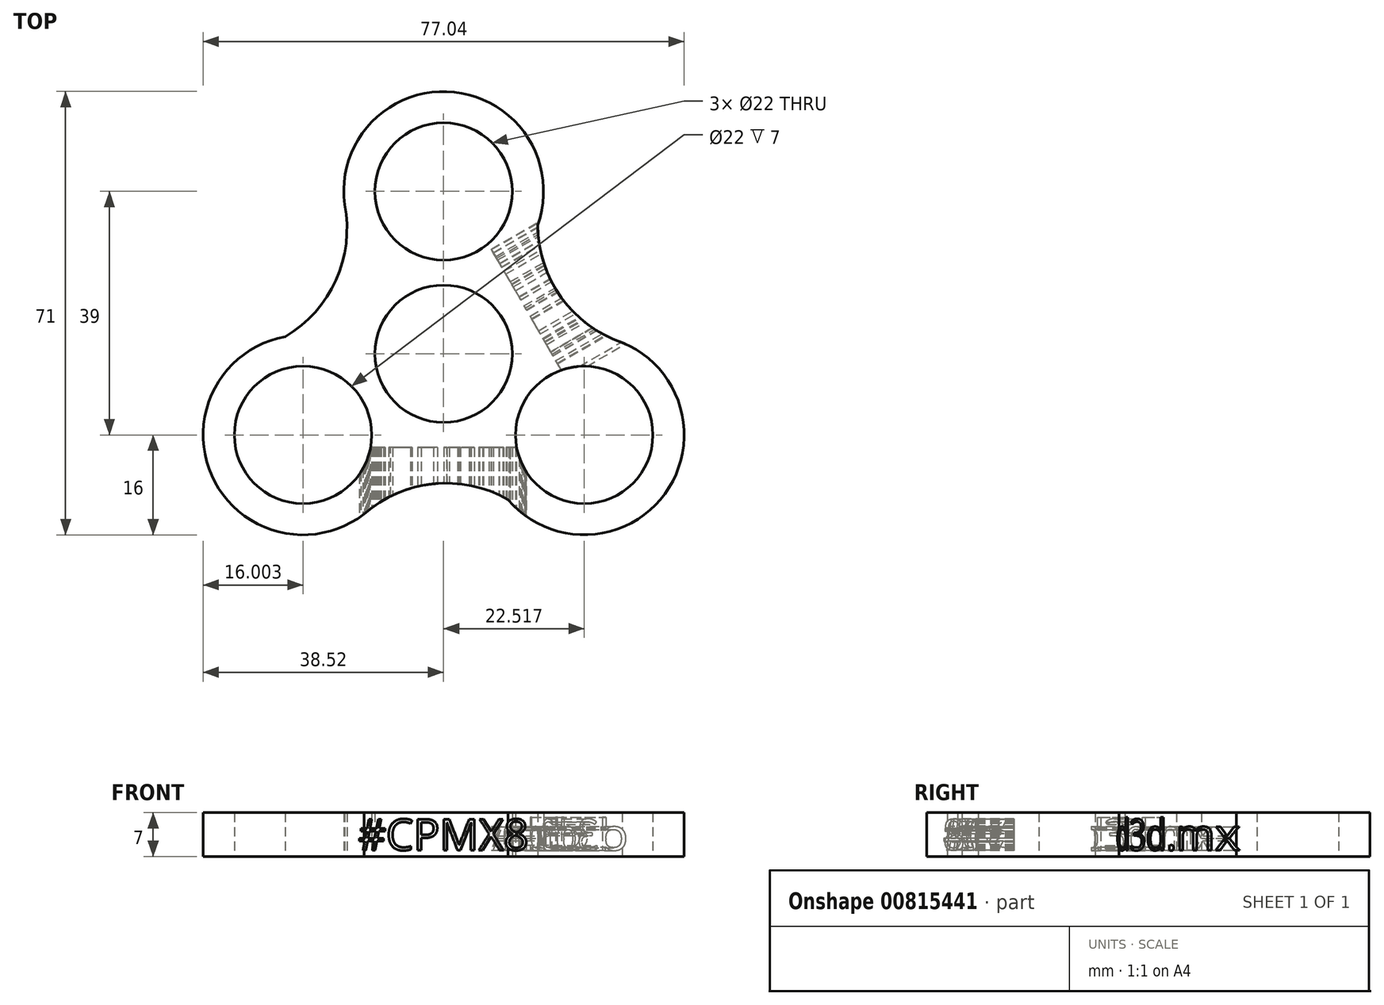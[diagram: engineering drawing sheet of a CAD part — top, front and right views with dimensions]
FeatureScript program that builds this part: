
annotation { "Feature Type Name" : "Feature", "Feature Type Description" : "" }
export const myFeature = defineFeature(function(context is Context, id is Id, definition is map)
    precondition{}
    {
        {
            var Q0;
            Q0=qCreatedBy(makeId("Top.planeOp"),FACE);
            var sketch = newSketch(context, id + "F0", { "sketchPlane" : qUnion([Q0])});
            skCircle(sketch, "E0", {"center": v(0, 0) * mm, "radius": 11 * mm});
            skCircle(sketch, "E1", {"center": v(0, 26) * mm, "radius": 11 * mm});
            skCircle(sketch, "E2.1.0", {"center": v(-22.52, -13) * mm, "radius": 11 * mm});
            skCircle(sketch, "E2.2.0", {"center": v(22.52, -13) * mm, "radius": 11 * mm});
            skArc(sketch, "E3", {"start": v(15.07, 20.61) * mm, "mid": v(1.13, 41.96) * mm, "end": v(-15.67, 22.78) * mm});
            skArc(sketch, "E4.1.0", {"start": v(-25.38, 2.74) * mm, "mid": v(-36.9, -20) * mm, "end": v(-11.9, -24.96) * mm});
            skArc(sketch, "E4.2.0", {"start": v(10.32, -23.35) * mm, "mid": v(35.77, -21.96) * mm, "end": v(27.57, 2.18) * mm});
            skArc(sketch, "E5", {"start": v(-25.38, 2.74) * mm, "mid": v(-17.24, 11.8) * mm, "end": v(-15.86, 23.89) * mm});
            skPoint(sketch, "E5.first.point", {"position": v(-25.38, 2.74) * mm});
            skPoint(sketch, "E5.second.point", {"position": v(-15.67, 22.78) * mm});
            skPoint(sketch, "E5.third.point", {"position": v(-55.07, 24.02) * mm});
            skArc(sketch, "E6.1.0", {"start": v(10.32, -23.35) * mm, "mid": v(-1.6, -20.83) * mm, "end": v(-12.76, -25.68) * mm});
            skArc(sketch, "E6.2.0", {"start": v(15.07, 20.61) * mm, "mid": v(18.84, 9.04) * mm, "end": v(28.62, 1.8) * mm});
            skSolve(sketch);
        }
        {
            var Q0;
            Q0=makeQuery(id+"F0.imprint","IMPRINT",FACE,{"disambiguationData":[TD([[makeQuery(id+"F0.imprint","IMPRINT",EDGE,{"derivedFrom":sQuery(id+"F0.wireOp",EDGE,"E0")}),-1.0]])]});
            extrude(context, id + "F1", {"entities" : qUnion([Q0]), "depth" : 7 * mm, "offsetDistance" : 25 * mm});
        }
        {
            var Q0;
            Q0=qCreatedBy(makeId("Front.planeOp"),FACE);
            cPlane(context, id + "F2", {"entities" : qUnion([Q0]), "cplaneType" : CPlaneType.OFFSET, "offset" : 30 * mm, "width" : 150 * mm, "height" : 150 * mm});
        }
        {
            var Q0;
            Q0=qCreatedBy(id+"F2.planeOp",FACE);
            var sketch = newSketch(context, id + "F3", { "sketchPlane" : qUnion([Q0])});
            skText(sketch, "E7", { "text": "#CPMX8", "fontName": "OpenSans-Regular.ttf"});
            const initialGuessF3  = {"E7": [-0.0137, 0.001, 1, 0, 0.005]};
            skSetInitialGuess(sketch, initialGuessF3);
            skSolve(sketch);
        }
        {
            var Q0;
            Q0 = qSketchRegion(id + "F3", true);
            extrude(context, id + "F4", {"entities" : qUnion([Q0]), "operationType" : NewBodyOperationType.REMOVE, "oppositeDirection" : true, "depth" : 15 * mm, "offsetDistance" : 25 * mm});
        }
        {
            var Q0;
            Q0=makeQuery(id+"F1.opExtrude","CAP_EDGE",EDGE,{"disambiguationData":[OSD([sQuery(id+"F0.wireOp",EDGE,"E0")])],"isStart":false});
            cPlane(context, id + "F5", {"entities" : qUnion([Q0]), "cplaneType" : CPlaneType.LINE_ANGLE, "offset" : 25 * mm, "angle" : 30 * degree, "width" : 150 * mm, "height" : 150 * mm});
        }
        {
            var Q0;
            Q0=qCreatedBy(id+"F5.planeOp",FACE);
            cPlane(context, id + "F6", {"entities" : qUnion([Q0]), "cplaneType" : CPlaneType.OFFSET, "offset" : 40 * mm, "width" : 150 * mm, "height" : 150 * mm});
        }
        {
            var Q0;
            Q0=qCreatedBy(id+"F6.planeOp",FACE);
            var sketch = newSketch(context, id + "F7", { "sketchPlane" : qUnion([Q0])});
            skText(sketch, "E8", { "text": "d3d.mx", "fontName": "OpenSans-Regular.ttf"});
            const initialGuessF7  = {"E8": [-0.0136, 0.001, 1, 0, 0.005]};
            skSetInitialGuess(sketch, initialGuessF7);
            skSolve(sketch);
        }
        {
            var Q0;
            Q0 = qSketchRegion(id + "F7", true);
            extrude(context, id + "F8", {"entities" : qUnion([Q0]), "operationType" : NewBodyOperationType.REMOVE, "oppositeDirection" : true, "depth" : 25 * mm, "offsetDistance" : 25 * mm});
        }
    });
